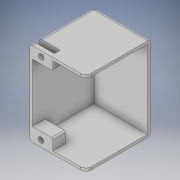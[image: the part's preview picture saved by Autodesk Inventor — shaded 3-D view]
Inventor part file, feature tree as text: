
AUTODESK INVENTOR PART (.ipt)
format: ipt  version: 2019 (Build 230136000, 136)  size: 222,720 bytes
history: native  units: mm
features: extrude x5, fillet x5, sketch x5, other x1, shell x1
ambient origin geometry x8: Origin, YZ Plane, XZ Plane, XY Plane, X Axis, Y Axis, Z Axis, Center Point
bodies: Body1 (feature_tree)
feature tree (17):
  other  "Sólido1"
  extrude  "Extrusão1"  Depth=47.0mm
  shell  "Casca1"  Thickness=61.0mm
  extrude  "Extrusão2"  Depth=13.0mm
  fillet  "Arredondamento4"  Radius=4.5mm
  extrude  "Extrusão8"  Depth=5.5mm
  extrude  "Extrusão9"  Depth=4.0mm
  extrude  "Extrusão10"  Depth=1.0mm
  fillet  "Arredondamento5"  Radius=3.8mm
  fillet  "Arredondamento6"  Radius=8.5mm
  fillet  "Arredondamento7"  Radius=3.0mm
  fillet  "Arredondamento10"  Radius=4.0mm
  sketch  "Esboço1"  dims[d0=41.0mm d1=47.0mm d2=61.0mm d3=0.0mm]
  sketch  "Esboço4"  dims[d4=2.0mm d15=13.0mm d16=4.5mm]
  sketch  "Esboço11"  dims[d17=13.0mm d18=5.5mm]
  sketch  "Esboço12"  dims[d19=4.0mm d20=4.0mm]
  sketch  "Esboço13"  dims[d21=4.5mm d22=8.3mm d23=3.8mm d24=8.5mm d25=3.0mm d26=0.0mm d33=4.0mm d47=4.2mm d48=4.2mm d49=13.0mm d50=2.0mm d51=0.0mm d52=0.0mm d53=2.0mm d54=10.0mm d55=9.2mm d56=2.0mm d57=13.0mm d58=0.0mm d59=2.0mm d60=0.0mm d61=2.0mm d62=2.0mm d63=2.0mm d66=1.0mm]
